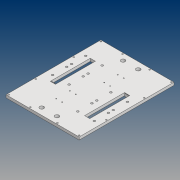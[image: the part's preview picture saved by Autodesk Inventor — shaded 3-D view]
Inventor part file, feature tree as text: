
AUTODESK INVENTOR PART (.ipt)
format: ipt  version: 2021 (Build 250183000, 183)  size: 262,656 bytes
history: native  units: mm
features: reference x32, other x13, sketch x6, hole x5, projected_geometry x3, extrude x2, mirror x2, pattern_circular x1
ambient origin geometry x8: Origin, YZ Plane, XZ Plane, XY Plane, X Axis, Y Axis, Z Axis, Center Point
bodies: Solid1 (feature_tree)
feature tree (64):
  extrude  "Extrusion1"  Depth=270.0mm
  hole  "Hole1"  [1 undecoded]
  mirror  "Mirror1"
  extrude  "Extrusion2"  Depth=100.0mm
  pattern_circular  "Circular Pattern1"  Count=10  [1 undecoded]
  sketch  "Sketch4"  dims[d8=80.0mm]
  hole  "Hole2"  [1 undecoded]
  hole  "Hole3"  [1 undecoded]
  hole  "Hole4"  [1 undecoded]
  hole  "Hole5"  [1 undecoded]
  mirror  "Mirror2"
  sketch  "Sketch1"  dims[d0=350.0mm d1=270.0mm]
  sketch  "Sketch2"  dims[d2=10.0mm d3=0.0mm d4=5.0mm]
  projected_geometry  "Projected Loop1"
  sketch  "Sketch3"  dims[d5=80.0mm d6=100.0mm d7=100.0mm]
  reference  "Reference1"
  reference  "Reference2"
  reference  "Reference3"
  reference  "Reference4"
  reference  "Reference5"
  reference  "Reference6"
  reference  "Reference7"
  reference  "Reference8"
  reference  "Reference9"
  reference  "Reference10"
  reference  "Reference11"
  reference  "Reference12"
  reference  "Reference13"
  reference  "Reference14"
  reference  "Reference15"
  reference  "Reference16"
  reference  "Reference17"
  reference  "Reference18"
  reference  "Reference19"
  reference  "Reference20"
  reference  "Reference21"
  reference  "Reference22"
  reference  "Reference23"
  reference  "Reference24"
  reference  "Reference25"
  reference  "Reference26"
  reference  "Reference27"
  reference  "Reference28"
  reference  "Reference29"
  reference  "Reference30"
  sketch  "Sketch5"  dims[d9=5.0mm d10=6.0mm d11=4.0mm d12=2.0mm d13=90.0deg d14=8.0mm d15=20.594885mm d16=0.0mm d17=0.0mm]
  projected_geometry  "Projected Loop2"
  sketch  "Sketch6"  dims[d18=2.0mm d19=20.0mm d20=360.0deg d22=0.5mm d23=0.5mm d24=7.5mm d25=6.0mm d26=4.0mm d27=2.0mm d28=90.0deg d29=8.0mm d30=20.594885mm d31=3.5mm d32=6.0mm d33=4.0mm d34=2.0mm d35=90.0deg d36=8.0mm d37=20.594885mm d38=56.0mm d39=30.0mm d40=15.0mm d41=6.0mm d42=4.0mm d43=2.0mm d44=90.0deg d45=8.0mm d46=20.594885mm d47=90.0mm d48=5.5mm d49=6.0mm d50=4.0mm d51=2.0mm d52=90.0deg d53=8.0mm d54=20.594885mm]
  projected_geometry  "Projected Loop3"
  reference  "Reference31"
  reference  "Reference32"
  other  "0001_ASS_Ban_lap_ghep_01.iam"
  other  "000ASS_Bo_banh_xe_04:1"
  other  "Spur Gear1:1"
  other  "Spur Gear2:1"
  other  "PK000:1"
  other  "PK000:2"
  other  "PK000:3"
  other  "PK000:4"
  other  "000ASS_Bo_banh_xe_04:2"
  other  "08_Ga_dong_co:1"
  other  "67060, ROLLER BALL BEARING:1"
  other  "67060, BODY, ROLLER BALL BEARING:1"
  other  "AS 1112 (2) - Metric M5  Type 5:2"
note: 6 required parameter values undecoded (feature->parameter linkage not recoverable at this tier; creation-order binding heuristic only, values carry confidence <= 0.55)
